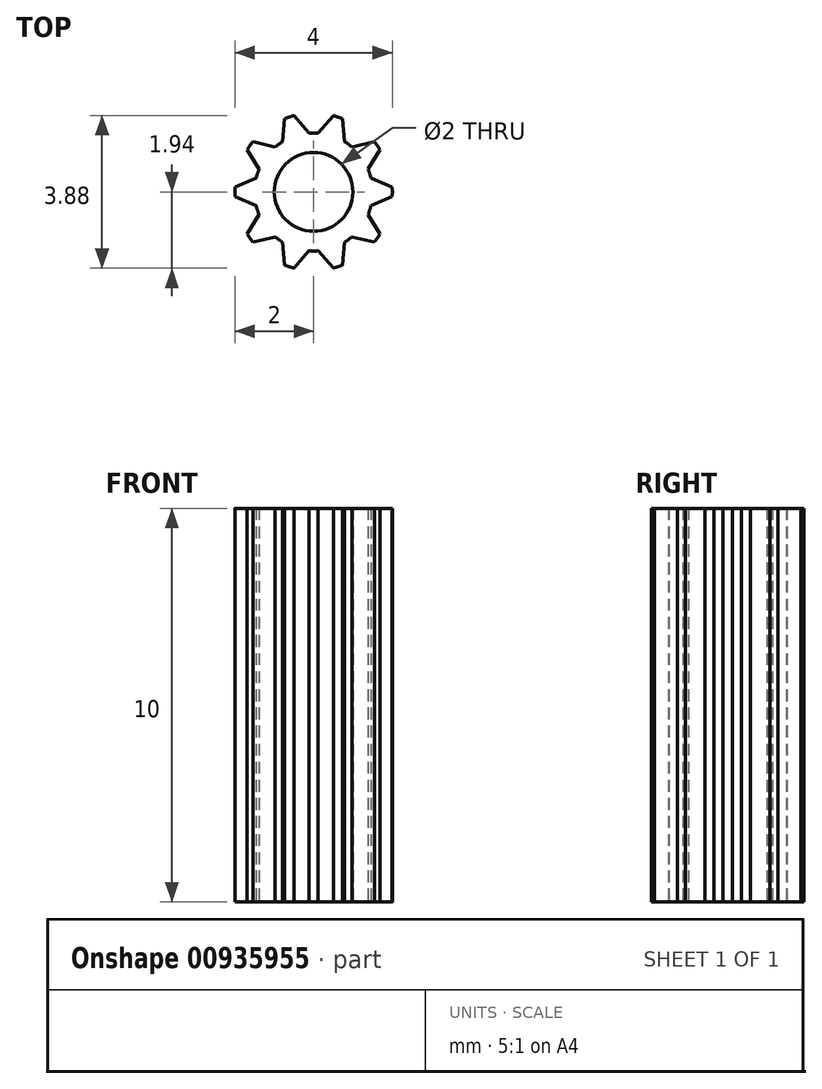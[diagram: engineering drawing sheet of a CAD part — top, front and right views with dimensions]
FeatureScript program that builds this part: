
annotation { "Feature Type Name" : "Feature", "Feature Type Description" : "" }
export const myFeature = defineFeature(function(context is Context, id is Id, definition is map)
    precondition{}
    {
        {
            var Q0;
            Q0=qCreatedBy(makeId("Top.planeOp"),FACE);
            var sketch = newSketch(context, id + "F0", { "sketchPlane" : qUnion([Q0])});
            skArc(sketch, "E0", {"start": v(-0.5, 1.94) * mm, "mid": v(0, -2) * mm, "end": v(0.5, 1.94) * mm});
            skCircle(sketch, "E1", {"center": v(0, 0) * mm, "radius": 1.5 * mm});
            skCircle(sketch, "E2", {"center": v(0, 0) * mm, "radius": 1 * mm});
            skLineSegment(sketch, "E3", {"start": v(-0.5, 1.94) * mm, "end": v(-0.12, 1.5) * mm});
            skLineSegment(sketch, "E4.MirrorCS", {"start": v(0.5, 1.94) * mm, "end": v(0.12, 1.5) * mm});
            skPoint(sketch, "E5.start.orphan", {"position": v(0, 2) * mm});
            skSolve(sketch);
        }
        {
            var Q0;
            Q0=makeQuery(id+"F0.imprint","IMPRINT",FACE,{"disambiguationData":[TD([[makeQuery(id+"F0.imprint","IMPRINT",EDGE,{"derivedFrom":sQuery(id+"F0.wireOp",EDGE,"E0")}),1.0]])]});
            var Q1;
            Q1=makeQuery(id+"F0.imprint","IMPRINT",FACE,{"disambiguationData":[TD([[makeQuery(id+"F0.imprint","IMPRINT",EDGE,{"derivedFrom":sQuery(id+"F0.wireOp",EDGE,"E2")}),-1.0]])]});
            extrude(context, id + "F1", {"entities" : qUnion([Q0, Q1]), "depth" : 10 * mm, "offsetDistance" : 25 * mm});
        }
        {
            var Q0;
            Q0=makeQuery(id+"F1.opExtrude","SWEPT_FACE",FACE,{"disambiguationData":[OSD([sQuery(id+"F0.wireOp",EDGE,"E3")])]});
            var Q1;
            Q1=makeQuery(id+"F1.opExtrude","SWEPT_FACE",FACE,{"disambiguationData":[OSD([sQuery(id+"F0.wireOp",EDGE,"E1")])]});
            var Q2;
            Q2=makeQuery(id+"F1.opExtrude","SWEPT_FACE",FACE,{"disambiguationData":[OSD([sQuery(id+"F0.wireOp",EDGE,"E4.MirrorCS")])]});
            var Q3;
            Q3=makeQuery(id+"F1.opExtrude","SWEPT_FACE",FACE,{"disambiguationData":[OSD([sQuery(id+"F0.wireOp",EDGE,"E0")])]});
            circularPattern(context, id + "F2", {"patternType" : PatternType.FACE, "faces" : qUnion([Q0, Q1, Q2]), "axis" : qUnion([Q3]), "angle" : 360 * degree, "instanceCount" : 10, "equalSpace" : true});
        }
    });
